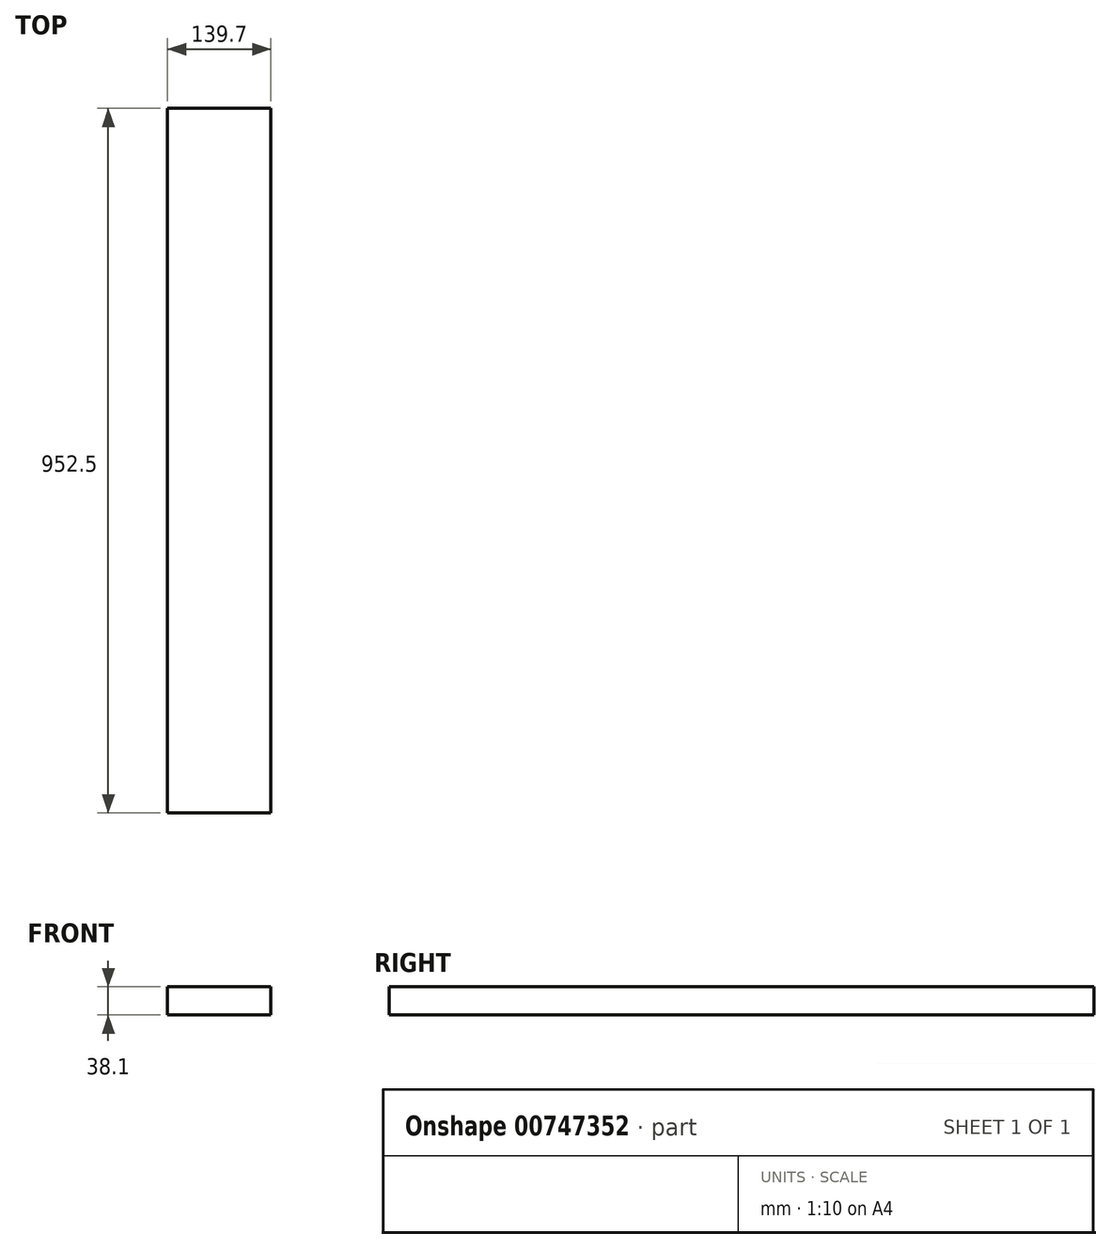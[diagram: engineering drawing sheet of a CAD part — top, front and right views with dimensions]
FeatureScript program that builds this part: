
annotation { "Feature Type Name" : "Feature", "Feature Type Description" : "" }
export const myFeature = defineFeature(function(context is Context, id is Id, definition is map)
    precondition{}
    {
        {
            var Q0;
            Q0=qCreatedBy(makeId("Front.planeOp"),FACE);
            var sketch = newSketch(context, id + "F0", { "sketchPlane" : qUnion([Q0])});
            skLineSegment(sketch, "E0.bottom", {"start": v(0, 0) * mm, "end": v(139.7, 0) * mm});
            skLineSegment(sketch, "E0.top", {"start": v(0, 38.1) * mm, "end": v(139.7, 38.1) * mm});
            skLineSegment(sketch, "E0.left", {"start": v(0, 0) * mm, "end": v(0, 38.1) * mm});
            skLineSegment(sketch, "E0.right", {"start": v(139.7, 0) * mm, "end": v(139.7, 38.1) * mm});
            skSolve(sketch);
        }
        {
            var Q0;
            Q0=qSketchRegion(id+"F0",true);
            extrude(context, id + "F1", {"entities" : qUnion([Q0]), "depth" : 952.5 * mm, "offsetDistance" : 25.4 * mm});
        }
    });
